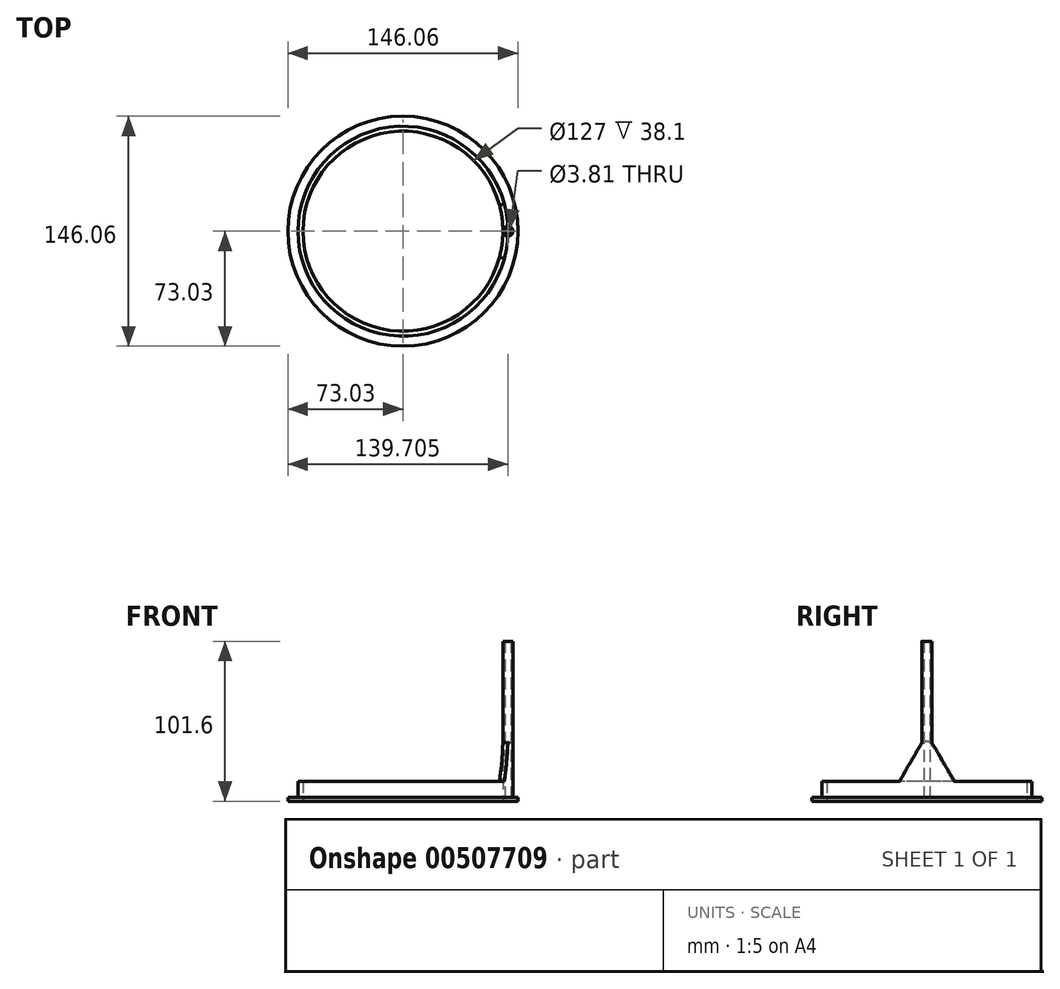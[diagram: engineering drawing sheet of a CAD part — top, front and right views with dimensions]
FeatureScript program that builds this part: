
annotation { "Feature Type Name" : "Feature", "Feature Type Description" : "" }
export const myFeature = defineFeature(function(context is Context, id is Id, definition is map)
    precondition{}
    {
        {
            var Q0;
            Q0=qCreatedBy(makeId("Top.planeOp"),FACE);
            var sketch = newSketch(context, id + "F0", { "sketchPlane" : qUnion([Q0])});
            skCircle(sketch, "E0", {"center": v(0, 0) * mm, "radius": 63.5 * mm});
            skCircle(sketch, "E1.0", {"center": v(0, 0) * mm, "radius": 66.67 * mm});
            skSolve(sketch);
        }
        {
            var Q0;
            Q0 = qSketchRegion(id + "F0", true);
            var Q1;
            Q1=sQuery(id+"F0.wireOp",EDGE,"E0");
            extrude(context, id + "F1", {"entities" : qUnion([Q0]), "surfaceEntities" : qUnion([Q1]), "depth" : 12.7 * mm});
        }
        {
            var Q0;
            Q0=qCreatedBy(makeId("Top.planeOp"),FACE);
            var sketch = newSketch(context, id + "F2", { "sketchPlane" : qUnion([Q0])});
            skCircle(sketch, "E2.0", {"center": v(0, 0) * mm, "radius": 73.02 * mm});
            skCircle(sketch, "E3.0", {"center": v(0, 0) * mm, "radius": 63.5 * mm});
            skSolve(sketch);
        }
        {
            var Q0;
            Q0 = qSketchRegion(id + "F2", true);
            extrude(context, id + "F3", {"entities" : qUnion([Q0]), "operationType" : NewBodyOperationType.ADD, "depth" : 2.54 * mm});
        }
        {
            var Q0;
            Q0=qCreatedBy(makeId("Top.planeOp"),FACE);
            var sketch = newSketch(context, id + "F4", { "sketchPlane" : qUnion([Q0])});
            skCircle(sketch, "E4", {"center": v(66.67, 0) * mm, "radius": 3.18 * mm});
            skSolve(sketch);
        }
        {
            var Q0;
            Q0 = qSketchRegion(id + "F4", true);
            extrude(context, id + "F5", {"entities" : qUnion([Q0]), "operationType" : NewBodyOperationType.ADD, "depth" : 101.6 * mm});
        }
        {
            var Q0;
            Q0=qCreatedBy(makeId("Top.planeOp"),FACE);
            var sketch = newSketch(context, id + "F6", { "sketchPlane" : qUnion([Q0])});
            skCircle(sketch, "E5.0", {"center": v(66.67, 0) * mm, "radius": 3.18 * mm, "construction": true});
            skCircle(sketch, "E6", {"center": v(66.67, 0) * mm, "radius": 1.9 * mm});
            skSolve(sketch);
        }
        {
            var Q0;
            Q0=makeQuery(id+"F1.opExtrude","CAP_FACE",FACE,{"disambiguationData":[OSD([sQuery(id+"F0.wireOp",EDGE,"E0"),sQuery(id+"F0.wireOp",EDGE,"E1.0")])],"isStart":false});
            var sketch = newSketch(context, id + "F7", { "sketchPlane" : qUnion([Q0])});
            skArc(sketch, "E7.0", {"start": v(61.34, -16.44) * mm, "mid": v(63.5, 0) * mm, "end": v(61.34, 16.44) * mm});
            skArc(sketch, "E7.1", {"start": v(66.6, 3.17) * mm, "mid": v(65.88, 10.27) * mm, "end": v(64.4, 17.26) * mm});
            skLineSegment(sketch, "E8", {"start": v(61.34, 16.44) * mm, "end": v(64.4, 17.26) * mm});
            skLineSegment(sketch, "E9", {"start": v(61.34, -16.44) * mm, "end": v(64.4, -17.26) * mm});
            skArc(sketch, "E10.trimOffspring", {"start": v(64.4, -17.26) * mm, "mid": v(66.3, -7.13) * mm, "end": v(66.6, 3.17) * mm});
            skPoint(sketch, "E11.orphan", {"position": v(66.6, -3.17) * mm});
            skSolve(sketch);
        }
        {
            var Q0;
            Q0 = qSketchRegion(id + "F7", true);
            extrude(context, id + "F8", {"entities" : qUnion([Q0]), "operationType" : NewBodyOperationType.ADD, "depth" : 25.4 * mm});
        }
        {
            var Q0;
            Q0=makeQuery(id+"F8.opExtrude","CAP_EDGE",EDGE,{"disambiguationData":[OSD([sQuery(id+"F7.wireOp",EDGE,"E9")])],"isStart":false});
            chamfer(context, id + "F9", {"entities" : qUnion([Q0]), "chamferType" : ChamferType.TWO_OFFSETS, "width1" : 14.73 * mm, "oppositeDirection" : false, "width2" : 25.15 * mm, "tangentPropagation" : true});
        }
        {
            var Q0;
            Q0=makeQuery(id+"F8.opExtrude","CAP_EDGE",EDGE,{"disambiguationData":[OSD([sQuery(id+"F7.wireOp",EDGE,"E8")])],"isStart":false});
            chamfer(context, id + "F10", {"entities" : qUnion([Q0]), "chamferType" : ChamferType.TWO_OFFSETS, "width1" : 24.9 * mm, "oppositeDirection" : false, "width2" : 14.73 * mm, "tangentPropagation" : true});
        }
        {
            var Q0;
            Q0 = qSketchRegion(id + "F6", true);
            var Q1;
            Q1 = qConstructionFilter(qBodyType(qCreatedBy(id + "F6" ,EDGE), BodyType.WIRE), ConstructionObject.NO);
            extrude(context, id + "F11", {"entities" : qUnion([Q0]), "operationType" : NewBodyOperationType.REMOVE, "surfaceEntities" : qUnion([Q1]), "endBound" : BoundingType.THROUGH_ALL, "depth" : 25.4 * mm});
        }
        {
            var Q0;
            Q0=makeQuery(id+"F8.boolean.opBoolean","INTERSECT",EDGE,{"disambiguationData":[OD(1.0)],"derivedFrom":[makeQuery(id+"F5.opExtrude","SWEPT_FACE",FACE,{"disambiguationData":[OSD([sQuery(id+"F4.wireOp",EDGE,"E4")])]}),makeQuery(id+"F8.opExtrude","SWEPT_FACE",FACE,{"disambiguationData":[OSD([sQuery(id+"F7.wireOp",EDGE,"E7.1"),sQuery(id+"F7.wireOp",EDGE,"E10.trimOffspring")])]})]});
            var Q1;
            Q1=makeQuery(id+"F8.boolean.opBoolean","INTERSECT",EDGE,{"disambiguationData":[OD(0.0)],"derivedFrom":[makeQuery(id+"F5.opExtrude","SWEPT_FACE",FACE,{"disambiguationData":[OSD([sQuery(id+"F4.wireOp",EDGE,"E4")])]}),makeQuery(id+"F8.opExtrude","SWEPT_FACE",FACE,{"disambiguationData":[OSD([sQuery(id+"F7.wireOp",EDGE,"E7.1"),sQuery(id+"F7.wireOp",EDGE,"E10.trimOffspring")])]})]});
            fillet(context, id + "F12", {"entities" : qUnion([Q0, Q1]), "radius" : 1.27 * mm, "tangentPropagation" : true, "allowEdgeOverflow" : false});
        }
        {
            var Q0;
            Q0=makeQuery(id+"F3.boolean.opBoolean","INTERSECT",EDGE,{"derivedFrom":[makeQuery(id+"F1.opExtrude","SWEPT_FACE",FACE,{"disambiguationData":[OSD([sQuery(id+"F0.wireOp",EDGE,"E1.0")])]}),makeQuery(id+"F3.opExtrude","CAP_FACE",FACE,{"disambiguationData":[OSD([sQuery(id+"F2.wireOp",EDGE,"E2.0"),sQuery(id+"F2.wireOp",EDGE,"E3.0")])],"isStart":false})]});
            fillet(context, id + "F13", {"entities" : qUnion([Q0]), "radius" : 1.27 * mm, "tangentPropagation" : true, "allowEdgeOverflow" : false});
        }
    });
